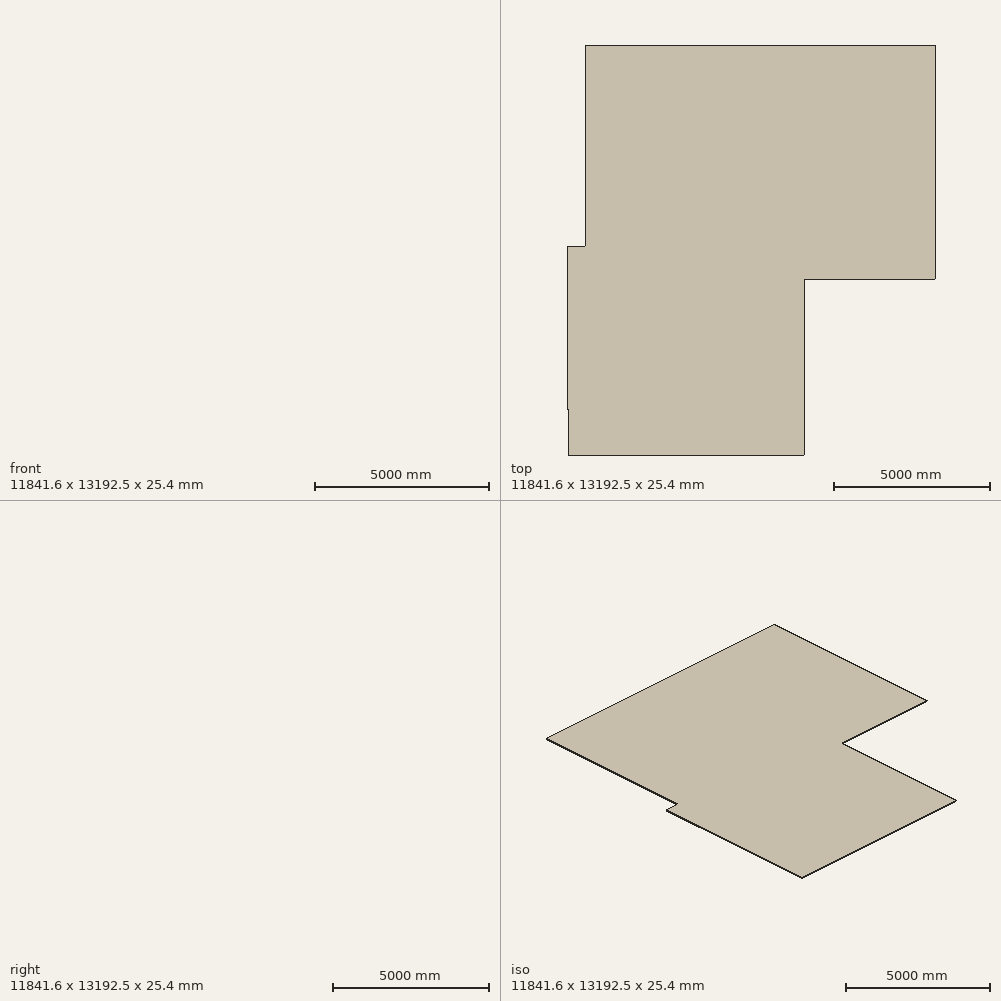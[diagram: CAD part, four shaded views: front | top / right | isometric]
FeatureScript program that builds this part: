
annotation { "Feature Type Name" : "Feature", "Feature Type Description" : "" }
export const myFeature = defineFeature(function(context is Context, id is Id, definition is map)
    precondition{}
    {
        {
            var Q0;
            Q0=qCreatedBy(makeId("Top.planeOp"),FACE);
            var sketch = newSketch(context, id + "F0", { "sketchPlane" : qUnion([Q0])});
            skLineSegment(sketch, "E0", {"start": v(-5865.85, -6575.23) * mm, "end": v(1754.15, -6575.23) * mm});
            skLineSegment(sketch, "E1", {"start": v(1754.15, -6575.23) * mm, "end": v(1754.15, -918.28) * mm});
            skLineSegment(sketch, "E2", {"start": v(1754.15, -918.28) * mm, "end": v(5954.65, -918.28) * mm});
            skLineSegment(sketch, "E3", {"start": v(5954.65, -918.28) * mm, "end": v(5954.65, 6617.29) * mm});
            skLineSegment(sketch, "E4", {"start": v(5954.65, 6617.29) * mm, "end": v(-5317.04, 6617.29) * mm});
            skLineSegment(sketch, "E5", {"start": v(-5317.04, 6617.29) * mm, "end": v(-5317.04, 137.12) * mm});
            skLineSegment(sketch, "E6", {"start": v(-5317.04, 137.12) * mm, "end": v(-5886.96, 137.12) * mm});
            skLineSegment(sketch, "E7", {"start": v(-5886.96, 137.12) * mm, "end": v(-5865.85, -6575.23) * mm});
            skSolve(sketch);
        }
        {
            var Q0;
            Q0=makeQuery(id+"F0.imprint","IMPRINT",FACE,{"disambiguationData":[TD([[makeQuery(id+"F0.imprint","IMPRINT",EDGE,{"derivedFrom":sQuery(id+"F0.wireOp",EDGE,"E0")}),1.0]])]});
            extrude(context, id + "F1", {"entities" : qUnion([Q0]), "depth" : 25.4 * mm, "offsetDistance" : 25.4 * mm});
        }
    });
